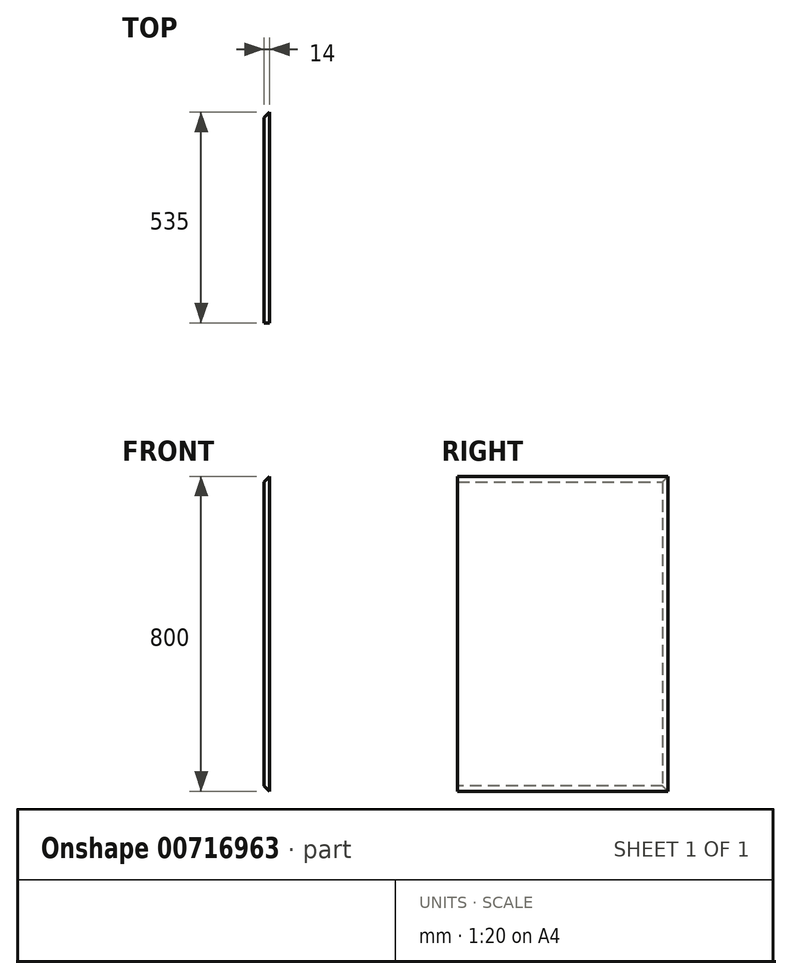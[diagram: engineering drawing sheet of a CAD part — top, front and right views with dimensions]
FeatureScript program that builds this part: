
annotation { "Feature Type Name" : "Feature", "Feature Type Description" : "" }
export const myFeature = defineFeature(function(context is Context, id is Id, definition is map)
    precondition{}
    {
        {
            var Q0;
            Q0=qCreatedBy(makeId("Right.planeOp"),FACE);
            var sketch = newSketch(context, id + "F0", { "sketchPlane" : qUnion([Q0])});
            skLineSegment(sketch, "E0.bottom", {"start": v(267.5, 400) * mm, "end": v(-267.5, 400) * mm});
            skLineSegment(sketch, "E0.top", {"start": v(267.5, -400) * mm, "end": v(-267.5, -400) * mm});
            skLineSegment(sketch, "E0.left", {"start": v(267.5, 400) * mm, "end": v(267.5, -400) * mm});
            skLineSegment(sketch, "E0.right", {"start": v(-267.5, 400) * mm, "end": v(-267.5, -400) * mm});
            skPoint(sketch, "E0.middle", {"position": v(0, 0) * mm});
            skSolve(sketch);
        }
        {
            var Q0;
            Q0=makeQuery(id+"F0.imprint","IMPRINT",FACE,{"disambiguationData":[TD([[makeQuery(id+"F0.imprint","IMPRINT",EDGE,{"derivedFrom":sQuery(id+"F0.wireOp",EDGE,"E0.bottom")}),1.0]])]});
            extrude(context, id + "F1", {"entities" : qUnion([Q0]), "depth" : 14 * mm, "offsetDistance" : 25 * mm});
        }
        {
            var Q0;
            Q0=makeQuery(id+"F1.opExtrude","CAP_EDGE",EDGE,{"disambiguationData":[OSD([sQuery(id+"F0.wireOp",EDGE,"E0.bottom")])],"isStart":true});
            var Q1;
            Q1=makeQuery(id+"F1.opExtrude","CAP_EDGE",EDGE,{"disambiguationData":[OSD([sQuery(id+"F0.wireOp",EDGE,"E0.left")])],"isStart":true});
            var Q2;
            Q2=makeQuery(id+"F1.opExtrude","CAP_EDGE",EDGE,{"disambiguationData":[OSD([sQuery(id+"F0.wireOp",EDGE,"E0.top")])],"isStart":true});
            chamfer(context, id + "F2", {"entities" : qUnion([Q0, Q1, Q2]), "width" : 14 * mm, "tangentPropagation" : true});
        }
    });
